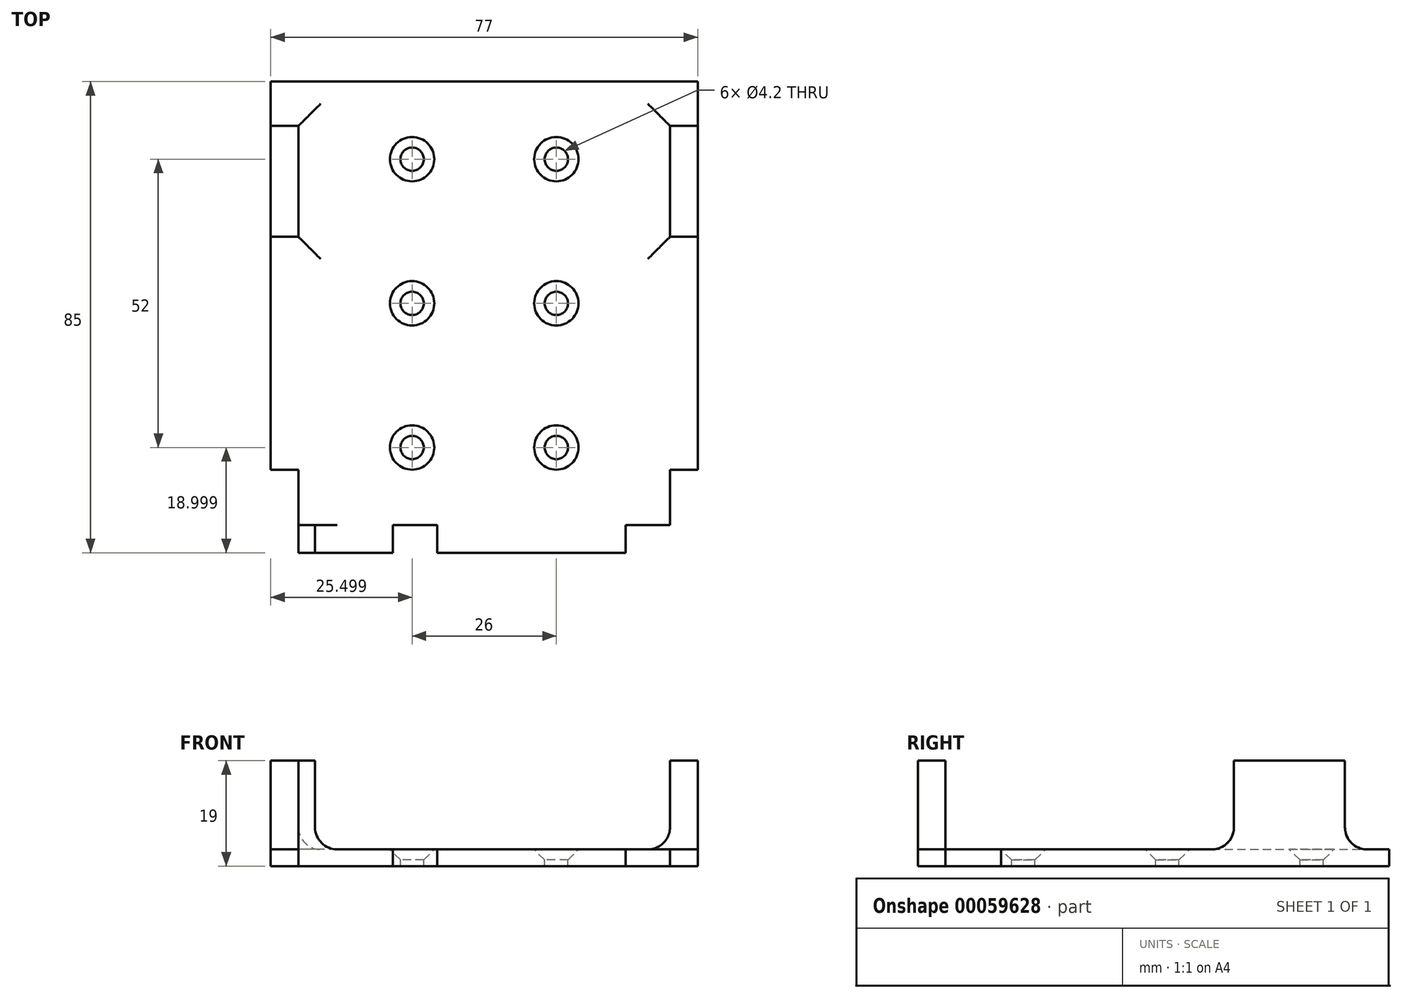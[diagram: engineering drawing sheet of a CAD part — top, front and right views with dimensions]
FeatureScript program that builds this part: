
annotation { "Feature Type Name" : "Feature", "Feature Type Description" : "" }
export const myFeature = defineFeature(function(context is Context, id is Id, definition is map)
    precondition{}
    {
        {
            var Q0;
            Q0=qCreatedBy(makeId("Top.planeOp"),FACE);
            var sketch = newSketch(context, id + "F0", { "sketchPlane" : qUnion([Q0])});
            skLineSegment(sketch, "E0.bottom", {"start": v(-19.43, 2.99) * mm, "end": v(57.57, 2.99) * mm});
            skLineSegment(sketch, "E0.top", {"start": v(-19.43, -82.01) * mm, "end": v(57.57, -82.01) * mm});
            skLineSegment(sketch, "E0.left", {"start": v(-19.43, 2.99) * mm, "end": v(-19.43, -82.01) * mm});
            skLineSegment(sketch, "E0.right", {"start": v(57.57, 2.99) * mm, "end": v(57.57, -82.01) * mm});
            skLineSegment(sketch, "E1.bottom", {"start": v(2.57, -82.01) * mm, "end": v(10.57, -82.01) * mm});
            skLineSegment(sketch, "E1.top", {"start": v(2.57, -77.01) * mm, "end": v(10.57, -77.01) * mm});
            skLineSegment(sketch, "E1.left", {"start": v(2.57, -82.01) * mm, "end": v(2.57, -77.01) * mm});
            skLineSegment(sketch, "E1.right", {"start": v(10.57, -82.01) * mm, "end": v(10.57, -77.01) * mm});
            skLineSegment(sketch, "E2.bottom", {"start": v(-19.43, -5.01) * mm, "end": v(-14.43, -5.01) * mm});
            skLineSegment(sketch, "E2.top", {"start": v(-19.43, -25.01) * mm, "end": v(-14.43, -25.01) * mm});
            skLineSegment(sketch, "E2.left", {"start": v(-19.43, -5.01) * mm, "end": v(-19.43, -25.01) * mm});
            skLineSegment(sketch, "E2.right", {"start": v(-14.43, -5.01) * mm, "end": v(-14.43, -25.01) * mm});
            skLineSegment(sketch, "E3.bottom", {"start": v(57.57, -5.01) * mm, "end": v(52.57, -5.01) * mm});
            skLineSegment(sketch, "E3.top", {"start": v(57.57, -25.01) * mm, "end": v(52.57, -25.01) * mm});
            skLineSegment(sketch, "E3.left", {"start": v(57.57, -5.01) * mm, "end": v(57.57, -25.01) * mm});
            skLineSegment(sketch, "E3.right", {"start": v(52.57, -5.01) * mm, "end": v(52.57, -25.01) * mm});
            skLineSegment(sketch, "E4", {"start": v(-14.43, -25.01) * mm, "end": v(-14.43, -108.86) * mm, "construction": true});
            skLineSegment(sketch, "E5", {"start": v(52.57, -25.01) * mm, "end": v(52.57, -106.5) * mm, "construction": true});
            skLineSegment(sketch, "E6", {"start": v(-41.42, -77.01) * mm, "end": v(97.95, -77.01) * mm, "construction": true});
            skPoint(sketch, "E7", {"position": v(-14.43, -77.01) * mm});
            skPoint(sketch, "E8", {"position": v(52.57, -77.01) * mm});
            skLineSegment(sketch, "E9.bottom", {"start": v(57.57, -82.01) * mm, "end": v(44.57, -82.01) * mm});
            skLineSegment(sketch, "E9.top", {"start": v(57.57, -77.01) * mm, "end": v(44.57, -77.01) * mm});
            skLineSegment(sketch, "E9.left", {"start": v(57.57, -82.01) * mm, "end": v(57.57, -77.01) * mm});
            skLineSegment(sketch, "E9.right", {"start": v(44.57, -82.01) * mm, "end": v(44.57, -77.01) * mm});
            skLineSegment(sketch, "E10.bottom", {"start": v(52.57, -77.01) * mm, "end": v(57.57, -77.01) * mm});
            skLineSegment(sketch, "E10.top", {"start": v(52.57, -67.01) * mm, "end": v(57.57, -67.01) * mm});
            skLineSegment(sketch, "E10.left", {"start": v(52.57, -77.01) * mm, "end": v(52.57, -67.01) * mm});
            skLineSegment(sketch, "E10.right", {"start": v(57.57, -77.01) * mm, "end": v(57.57, -67.01) * mm});
            skLineSegment(sketch, "E11.bottom", {"start": v(-19.43, -82.01) * mm, "end": v(-14.43, -82.01) * mm});
            skLineSegment(sketch, "E11.top", {"start": v(-19.43, -67.01) * mm, "end": v(-14.43, -67.01) * mm});
            skLineSegment(sketch, "E11.left", {"start": v(-19.43, -82.01) * mm, "end": v(-19.43, -67.01) * mm});
            skLineSegment(sketch, "E11.right", {"start": v(-14.43, -82.01) * mm, "end": v(-14.43, -67.01) * mm});
            skLineSegment(sketch, "E12.bottom", {"start": v(-14.43, -77.01) * mm, "end": v(-11.43, -77.01) * mm});
            skLineSegment(sketch, "E12.top", {"start": v(-14.43, -82.01) * mm, "end": v(-11.43, -82.01) * mm});
            skLineSegment(sketch, "E12.left", {"start": v(-14.43, -77.01) * mm, "end": v(-14.43, -82.01) * mm});
            skLineSegment(sketch, "E12.right", {"start": v(-11.43, -77.01) * mm, "end": v(-11.43, -82.01) * mm});
            skLineSegment(sketch, "E13", {"start": v(19.07, 2.99) * mm, "end": v(19.07, -82.01) * mm, "construction": true});
            skCircle(sketch, "E14", {"center": v(19.07, -11.01) * mm, "radius": 13 * mm, "construction": true});
            skCircle(sketch, "E15", {"center": v(6.07, -11.01) * mm, "radius": 1.6 * mm, "construction": true});
            skCircle(sketch, "E16", {"center": v(32.07, -11.01) * mm, "radius": 1.6 * mm, "construction": true});
            skCircle(sketch, "E17", {"center": v(19.07, -63.01) * mm, "radius": 13 * mm, "construction": true});
            skCircle(sketch, "E18", {"center": v(32.07, -63.01) * mm, "radius": 1.6 * mm, "construction": true});
            skCircle(sketch, "E19", {"center": v(6.07, -63.01) * mm, "radius": 1.6 * mm, "construction": true});
            skCircle(sketch, "E20", {"center": v(19.07, -37.01) * mm, "radius": 13 * mm, "construction": true});
            skLineSegment(sketch, "E21", {"start": v(6.07, -37.01) * mm, "end": v(32.07, -37.01) * mm, "construction": true});
            skCircle(sketch, "E22", {"center": v(6.07, -37.01) * mm, "radius": 1.6 * mm, "construction": true});
            skCircle(sketch, "E23", {"center": v(32.07, -37.01) * mm, "radius": 1.6 * mm, "construction": true});
            skSolve(sketch);
        }
        {
            var Q0;
            {var subQ7=sQuery(id+"F0.wireOp",EDGE,"E0.bottom");Q0=makeQuery(id+"F0.imprint","IMPRINT",FACE,{"disambiguationData":[TD([[makeQuery(id+"F0.imprint","IMPRINT",EDGE,{"derivedFrom":subQ7}),-1.0]])]});}
            var Q1;
            Q1=makeQuery(id+"F0.imprint","IMPRINT",FACE,{"disambiguationData":[TD([[makeQuery(id+"F0.imprint","IMPRINT",EDGE,{"derivedFrom":sQuery(id+"F0.wireOp",EDGE,"E1.bottom")}),1.0]])]});
            var Q2;
            Q2=makeQuery(id+"F0.imprint","IMPRINT",FACE,{"disambiguationData":[TD([[makeQuery(id+"F0.imprint","IMPRINT",EDGE,{"derivedFrom":sQuery(id+"F0.wireOp",EDGE,"E11.bottom")}),1.0]])]});
            var Q3;
            Q3=makeQuery(id+"F0.imprint","IMPRINT",FACE,{"disambiguationData":[TD([[makeQuery(id+"F0.imprint","IMPRINT",EDGE,{"derivedFrom":sQuery(id+"F0.wireOp",EDGE,"E12.bottom")}),-1.0]])]});
            var Q4;
            Q4=makeQuery(id+"F0.imprint","IMPRINT",FACE,{"disambiguationData":[TD([[makeQuery(id+"F0.imprint","IMPRINT",EDGE,{"derivedFrom":sQuery(id+"F0.wireOp",EDGE,"E9.bottom")}),-1.0]])]});
            var Q5;
            Q5=makeQuery(id+"F0.imprint","IMPRINT",FACE,{"disambiguationData":[TD([[makeQuery(id+"F0.imprint","IMPRINT",EDGE,{"derivedFrom":sQuery(id+"F0.wireOp",EDGE,"E10.bottom")}),1.0]])]});
            var Q6;
            Q6=makeQuery(id+"F0.imprint","IMPRINT",FACE,{"disambiguationData":[TD([[makeQuery(id+"F0.imprint","IMPRINT",EDGE,{"derivedFrom":sQuery(id+"F0.wireOp",EDGE,"E3.bottom")}),1.0]])]});
            var Q7;
            Q7=makeQuery(id+"F0.imprint","IMPRINT",FACE,{"disambiguationData":[TD([[makeQuery(id+"F0.imprint","IMPRINT",EDGE,{"derivedFrom":sQuery(id+"F0.wireOp",EDGE,"E2.bottom")}),-1.0]])]});
            extrude(context, id + "F1", {"entities" : qUnion([Q0, Q1, Q2, Q3, Q4, Q5, Q6, Q7]), "depth" : 3 * mm});
        }
        {
            var Q0;
            Q0=makeQuery(id+"F0.imprint","IMPRINT",FACE,{"disambiguationData":[TD([[makeQuery(id+"F0.imprint","IMPRINT",EDGE,{"derivedFrom":sQuery(id+"F0.wireOp",EDGE,"E2.bottom")}),-1.0]])]});
            var Q1;
            Q1=makeQuery(id+"F0.imprint","IMPRINT",FACE,{"disambiguationData":[TD([[makeQuery(id+"F0.imprint","IMPRINT",EDGE,{"derivedFrom":sQuery(id+"F0.wireOp",EDGE,"E3.bottom")}),1.0]])]});
            var Q2;
            Q2=makeQuery(id+"F0.imprint","IMPRINT",FACE,{"disambiguationData":[TD([[makeQuery(id+"F0.imprint","IMPRINT",EDGE,{"derivedFrom":sQuery(id+"F0.wireOp",EDGE,"E10.bottom")}),1.0]])]});
            var Q3;
            Q3=makeQuery(id+"F0.imprint","IMPRINT",FACE,{"disambiguationData":[TD([[makeQuery(id+"F0.imprint","IMPRINT",EDGE,{"derivedFrom":sQuery(id+"F0.wireOp",EDGE,"E9.bottom")}),-1.0]])]});
            var Q4;
            Q4=makeQuery(id+"F0.imprint","IMPRINT",FACE,{"disambiguationData":[TD([[makeQuery(id+"F0.imprint","IMPRINT",EDGE,{"derivedFrom":sQuery(id+"F0.wireOp",EDGE,"E1.bottom")}),1.0]])]});
            var Q5;
            Q5=makeQuery(id+"F0.imprint","IMPRINT",FACE,{"disambiguationData":[TD([[makeQuery(id+"F0.imprint","IMPRINT",EDGE,{"derivedFrom":sQuery(id+"F0.wireOp",EDGE,"E11.bottom")}),1.0]])]});
            var Q6;
            Q6=makeQuery(id+"F0.imprint","IMPRINT",FACE,{"disambiguationData":[TD([[makeQuery(id+"F0.imprint","IMPRINT",EDGE,{"derivedFrom":sQuery(id+"F0.wireOp",EDGE,"E12.bottom")}),-1.0]])]});
            extrude(context, id + "F2", {"entities" : qUnion([Q0, Q1, Q2, Q3, Q4, Q5, Q6]), "operationType" : NewBodyOperationType.ADD, "depth" : 19 * mm});
        }
        {
            var Q0;
            Q0=makeQuery(id+"F1.opExtrude","CAP_FACE",FACE,{"disambiguationData":[OSD([sQuery(id+"F0.wireOp",EDGE,"E0.bottom"),sQuery(id+"F0.wireOp",EDGE,"E0.top"),sQuery(id+"F0.wireOp",EDGE,"E0.left"),sQuery(id+"F0.wireOp",EDGE,"E0.right"),sQuery(id+"F0.wireOp",EDGE,"E1.bottom"),sQuery(id+"F0.wireOp",EDGE,"E2.left"),sQuery(id+"F0.wireOp",EDGE,"E3.left"),sQuery(id+"F0.wireOp",EDGE,"E9.bottom"),sQuery(id+"F0.wireOp",EDGE,"E9.left"),sQuery(id+"F0.wireOp",EDGE,"E10.right"),sQuery(id+"F0.wireOp",EDGE,"E11.bottom"),sQuery(id+"F0.wireOp",EDGE,"E11.left"),sQuery(id+"F0.wireOp",EDGE,"E12.top")])],"isStart":false});
            var sketch = newSketch(context, id + "F3", { "sketchPlane" : qUnion([Q0])});
            skPoint(sketch, "E24", {"position": v(6.07, -11.01) * mm});
            skPoint(sketch, "E25", {"position": v(32.07, -11.01) * mm});
            skPoint(sketch, "E26", {"position": v(6.07, -63.01) * mm});
            skPoint(sketch, "E27", {"position": v(32.07, -63.01) * mm});
            skPoint(sketch, "E28", {"position": v(6.07, -37.01) * mm});
            skPoint(sketch, "E29", {"position": v(32.07, -37.01) * mm});
            skSolve(sketch);
        }
        {
            var Q0;
            Q0=sQuery(id+"F3.wireOp",VERTEX,"E24");
            var Q1;
            Q1=sQuery(id+"F3.wireOp",VERTEX,"E25");
            var Q2;
            Q2=sQuery(id+"F3.wireOp",VERTEX,"E26");
            var Q3;
            Q3=sQuery(id+"F3.wireOp",VERTEX,"E27");
            var Q4;
            Q4=sQuery(id+"F3.wireOp",VERTEX,"E29");
            var Q5;
            Q5=sQuery(id+"F3.wireOp",VERTEX,"E28");
            var Q6;
            Q6=makeQuery(id+"F1.opExtrude","SWEPT_BODY",BODY,{"disambiguationData":[OSD([sQuery(id+"F0.wireOp",EDGE,"E0.bottom"),sQuery(id+"F0.wireOp",EDGE,"E0.top"),sQuery(id+"F0.wireOp",EDGE,"E0.left"),sQuery(id+"F0.wireOp",EDGE,"E0.right"),sQuery(id+"F0.wireOp",EDGE,"E1.bottom"),sQuery(id+"F0.wireOp",EDGE,"E2.left"),sQuery(id+"F0.wireOp",EDGE,"E3.left"),sQuery(id+"F0.wireOp",EDGE,"E9.bottom"),sQuery(id+"F0.wireOp",EDGE,"E9.left"),sQuery(id+"F0.wireOp",EDGE,"E10.right"),sQuery(id+"F0.wireOp",EDGE,"E11.bottom"),sQuery(id+"F0.wireOp",EDGE,"E11.left"),sQuery(id+"F0.wireOp",EDGE,"E12.top")])]});
            hole(context, id + "F4", {"style" : HoleStyle.C_SINK, "holeDiameter" : 4.2 * mm, "cSinkDiameter" : 8 * mm, "endStyle" : HoleEndStyle.THROUGH, "locations" : qUnion([Q0, Q1, Q2, Q3, Q4, Q5]), "scope" : qUnion([Q6]), "cSinkAngle" : 90 * degree, "tappedDepth" : 12 * mm, "tapClearance" : 3});
        }
        {
            var Q0;
            Q0=makeQuery(id+"F2.boolean.opBoolean","INTERSECT",EDGE,{"derivedFrom":[makeQuery(id+"F1.opExtrude","CAP_FACE",FACE,{"disambiguationData":[OSD([sQuery(id+"F0.wireOp",EDGE,"E0.bottom"),sQuery(id+"F0.wireOp",EDGE,"E0.top"),sQuery(id+"F0.wireOp",EDGE,"E0.left"),sQuery(id+"F0.wireOp",EDGE,"E0.right"),sQuery(id+"F0.wireOp",EDGE,"E1.bottom"),sQuery(id+"F0.wireOp",EDGE,"E2.left"),sQuery(id+"F0.wireOp",EDGE,"E3.left"),sQuery(id+"F0.wireOp",EDGE,"E9.bottom"),sQuery(id+"F0.wireOp",EDGE,"E9.left"),sQuery(id+"F0.wireOp",EDGE,"E10.right"),sQuery(id+"F0.wireOp",EDGE,"E11.bottom"),sQuery(id+"F0.wireOp",EDGE,"E11.left"),sQuery(id+"F0.wireOp",EDGE,"E12.top")])],"isStart":false}),makeQuery(id+"F2.opExtrude","SWEPT_FACE",FACE,{"disambiguationData":[OSD([sQuery(id+"F0.wireOp",EDGE,"E2.top")])]})]});
            var Q1;
            Q1=makeQuery(id+"F2.boolean.opBoolean","INTERSECT",EDGE,{"derivedFrom":[makeQuery(id+"F1.opExtrude","CAP_FACE",FACE,{"disambiguationData":[OSD([sQuery(id+"F0.wireOp",EDGE,"E0.bottom"),sQuery(id+"F0.wireOp",EDGE,"E0.top"),sQuery(id+"F0.wireOp",EDGE,"E0.left"),sQuery(id+"F0.wireOp",EDGE,"E0.right"),sQuery(id+"F0.wireOp",EDGE,"E1.bottom"),sQuery(id+"F0.wireOp",EDGE,"E2.left"),sQuery(id+"F0.wireOp",EDGE,"E3.left"),sQuery(id+"F0.wireOp",EDGE,"E9.bottom"),sQuery(id+"F0.wireOp",EDGE,"E9.left"),sQuery(id+"F0.wireOp",EDGE,"E10.right"),sQuery(id+"F0.wireOp",EDGE,"E11.bottom"),sQuery(id+"F0.wireOp",EDGE,"E11.left"),sQuery(id+"F0.wireOp",EDGE,"E12.top")])],"isStart":false}),makeQuery(id+"F2.opExtrude","SWEPT_FACE",FACE,{"disambiguationData":[OSD([sQuery(id+"F0.wireOp",EDGE,"E11.top")])]})]});
            var Q2;
            Q2=makeQuery(id+"F2.boolean.opBoolean","INTERSECT",EDGE,{"derivedFrom":[makeQuery(id+"F1.opExtrude","CAP_FACE",FACE,{"disambiguationData":[OSD([sQuery(id+"F0.wireOp",EDGE,"E0.bottom"),sQuery(id+"F0.wireOp",EDGE,"E0.top"),sQuery(id+"F0.wireOp",EDGE,"E0.left"),sQuery(id+"F0.wireOp",EDGE,"E0.right"),sQuery(id+"F0.wireOp",EDGE,"E1.bottom"),sQuery(id+"F0.wireOp",EDGE,"E2.left"),sQuery(id+"F0.wireOp",EDGE,"E3.left"),sQuery(id+"F0.wireOp",EDGE,"E9.bottom"),sQuery(id+"F0.wireOp",EDGE,"E9.left"),sQuery(id+"F0.wireOp",EDGE,"E10.right"),sQuery(id+"F0.wireOp",EDGE,"E11.bottom"),sQuery(id+"F0.wireOp",EDGE,"E11.left"),sQuery(id+"F0.wireOp",EDGE,"E12.top")])],"isStart":false}),makeQuery(id+"F2.opExtrude","SWEPT_FACE",FACE,{"disambiguationData":[OSD([sQuery(id+"F0.wireOp",EDGE,"E12.right")])]})]});
            var Q3;
            Q3=makeQuery(id+"F2.boolean.opBoolean","INTERSECT",EDGE,{"derivedFrom":[makeQuery(id+"F1.opExtrude","CAP_FACE",FACE,{"disambiguationData":[OSD([sQuery(id+"F0.wireOp",EDGE,"E0.bottom"),sQuery(id+"F0.wireOp",EDGE,"E0.top"),sQuery(id+"F0.wireOp",EDGE,"E0.left"),sQuery(id+"F0.wireOp",EDGE,"E0.right"),sQuery(id+"F0.wireOp",EDGE,"E1.bottom"),sQuery(id+"F0.wireOp",EDGE,"E2.left"),sQuery(id+"F0.wireOp",EDGE,"E3.left"),sQuery(id+"F0.wireOp",EDGE,"E9.bottom"),sQuery(id+"F0.wireOp",EDGE,"E9.left"),sQuery(id+"F0.wireOp",EDGE,"E10.right"),sQuery(id+"F0.wireOp",EDGE,"E11.bottom"),sQuery(id+"F0.wireOp",EDGE,"E11.left"),sQuery(id+"F0.wireOp",EDGE,"E12.top")])],"isStart":false}),makeQuery(id+"F2.opExtrude","SWEPT_FACE",FACE,{"disambiguationData":[OSD([sQuery(id+"F0.wireOp",EDGE,"E1.right")])]})]});
            var Q4;
            Q4=makeQuery(id+"F2.boolean.opBoolean","INTERSECT",EDGE,{"derivedFrom":[makeQuery(id+"F1.opExtrude","CAP_FACE",FACE,{"disambiguationData":[OSD([sQuery(id+"F0.wireOp",EDGE,"E0.bottom"),sQuery(id+"F0.wireOp",EDGE,"E0.top"),sQuery(id+"F0.wireOp",EDGE,"E0.left"),sQuery(id+"F0.wireOp",EDGE,"E0.right"),sQuery(id+"F0.wireOp",EDGE,"E1.bottom"),sQuery(id+"F0.wireOp",EDGE,"E2.left"),sQuery(id+"F0.wireOp",EDGE,"E3.left"),sQuery(id+"F0.wireOp",EDGE,"E9.bottom"),sQuery(id+"F0.wireOp",EDGE,"E9.left"),sQuery(id+"F0.wireOp",EDGE,"E10.right"),sQuery(id+"F0.wireOp",EDGE,"E11.bottom"),sQuery(id+"F0.wireOp",EDGE,"E11.left"),sQuery(id+"F0.wireOp",EDGE,"E12.top")])],"isStart":false}),makeQuery(id+"F2.opExtrude","SWEPT_FACE",FACE,{"disambiguationData":[OSD([sQuery(id+"F0.wireOp",EDGE,"E1.left")])]})]});
            var Q5;
            Q5=makeQuery(id+"F2.boolean.opBoolean","INTERSECT",EDGE,{"derivedFrom":[makeQuery(id+"F1.opExtrude","CAP_FACE",FACE,{"disambiguationData":[OSD([sQuery(id+"F0.wireOp",EDGE,"E0.bottom"),sQuery(id+"F0.wireOp",EDGE,"E0.top"),sQuery(id+"F0.wireOp",EDGE,"E0.left"),sQuery(id+"F0.wireOp",EDGE,"E0.right"),sQuery(id+"F0.wireOp",EDGE,"E1.bottom"),sQuery(id+"F0.wireOp",EDGE,"E2.left"),sQuery(id+"F0.wireOp",EDGE,"E3.left"),sQuery(id+"F0.wireOp",EDGE,"E9.bottom"),sQuery(id+"F0.wireOp",EDGE,"E9.left"),sQuery(id+"F0.wireOp",EDGE,"E10.right"),sQuery(id+"F0.wireOp",EDGE,"E11.bottom"),sQuery(id+"F0.wireOp",EDGE,"E11.left"),sQuery(id+"F0.wireOp",EDGE,"E12.top")])],"isStart":false}),makeQuery(id+"F2.opExtrude","SWEPT_FACE",FACE,{"disambiguationData":[OSD([sQuery(id+"F0.wireOp",EDGE,"E9.right")])]})]});
            var Q6;
            Q6=makeQuery(id+"F2.boolean.opBoolean","INTERSECT",EDGE,{"derivedFrom":[makeQuery(id+"F1.opExtrude","CAP_FACE",FACE,{"disambiguationData":[OSD([sQuery(id+"F0.wireOp",EDGE,"E0.bottom"),sQuery(id+"F0.wireOp",EDGE,"E0.top"),sQuery(id+"F0.wireOp",EDGE,"E0.left"),sQuery(id+"F0.wireOp",EDGE,"E0.right"),sQuery(id+"F0.wireOp",EDGE,"E1.bottom"),sQuery(id+"F0.wireOp",EDGE,"E2.left"),sQuery(id+"F0.wireOp",EDGE,"E3.left"),sQuery(id+"F0.wireOp",EDGE,"E9.bottom"),sQuery(id+"F0.wireOp",EDGE,"E9.left"),sQuery(id+"F0.wireOp",EDGE,"E10.right"),sQuery(id+"F0.wireOp",EDGE,"E11.bottom"),sQuery(id+"F0.wireOp",EDGE,"E11.left"),sQuery(id+"F0.wireOp",EDGE,"E12.top")])],"isStart":false}),makeQuery(id+"F2.opExtrude","SWEPT_FACE",FACE,{"disambiguationData":[OSD([sQuery(id+"F0.wireOp",EDGE,"E3.top")])]})]});
            var Q7;
            Q7=makeQuery(id+"F2.boolean.opBoolean","INTERSECT",EDGE,{"derivedFrom":[makeQuery(id+"F1.opExtrude","CAP_FACE",FACE,{"disambiguationData":[OSD([sQuery(id+"F0.wireOp",EDGE,"E0.bottom"),sQuery(id+"F0.wireOp",EDGE,"E0.top"),sQuery(id+"F0.wireOp",EDGE,"E0.left"),sQuery(id+"F0.wireOp",EDGE,"E0.right"),sQuery(id+"F0.wireOp",EDGE,"E1.bottom"),sQuery(id+"F0.wireOp",EDGE,"E2.left"),sQuery(id+"F0.wireOp",EDGE,"E3.left"),sQuery(id+"F0.wireOp",EDGE,"E9.bottom"),sQuery(id+"F0.wireOp",EDGE,"E9.left"),sQuery(id+"F0.wireOp",EDGE,"E10.right"),sQuery(id+"F0.wireOp",EDGE,"E11.bottom"),sQuery(id+"F0.wireOp",EDGE,"E11.left"),sQuery(id+"F0.wireOp",EDGE,"E12.top")])],"isStart":false}),makeQuery(id+"F2.opExtrude","SWEPT_FACE",FACE,{"disambiguationData":[OSD([sQuery(id+"F0.wireOp",EDGE,"E10.top")])]})]});
            var Q8;
            Q8=makeQuery(id+"F2.boolean.opBoolean","INTERSECT",EDGE,{"derivedFrom":[makeQuery(id+"F1.opExtrude","CAP_FACE",FACE,{"disambiguationData":[OSD([sQuery(id+"F0.wireOp",EDGE,"E0.bottom"),sQuery(id+"F0.wireOp",EDGE,"E0.top"),sQuery(id+"F0.wireOp",EDGE,"E0.left"),sQuery(id+"F0.wireOp",EDGE,"E0.right"),sQuery(id+"F0.wireOp",EDGE,"E1.bottom"),sQuery(id+"F0.wireOp",EDGE,"E2.left"),sQuery(id+"F0.wireOp",EDGE,"E3.left"),sQuery(id+"F0.wireOp",EDGE,"E9.bottom"),sQuery(id+"F0.wireOp",EDGE,"E9.left"),sQuery(id+"F0.wireOp",EDGE,"E10.right"),sQuery(id+"F0.wireOp",EDGE,"E11.bottom"),sQuery(id+"F0.wireOp",EDGE,"E11.left"),sQuery(id+"F0.wireOp",EDGE,"E12.top")])],"isStart":false}),makeQuery(id+"F2.opExtrude","SWEPT_FACE",FACE,{"disambiguationData":[OSD([sQuery(id+"F0.wireOp",EDGE,"E3.bottom")])]})]});
            var Q9;
            Q9=makeQuery(id+"F2.boolean.opBoolean","INTERSECT",EDGE,{"derivedFrom":[makeQuery(id+"F1.opExtrude","CAP_FACE",FACE,{"disambiguationData":[OSD([sQuery(id+"F0.wireOp",EDGE,"E0.bottom"),sQuery(id+"F0.wireOp",EDGE,"E0.top"),sQuery(id+"F0.wireOp",EDGE,"E0.left"),sQuery(id+"F0.wireOp",EDGE,"E0.right"),sQuery(id+"F0.wireOp",EDGE,"E1.bottom"),sQuery(id+"F0.wireOp",EDGE,"E2.left"),sQuery(id+"F0.wireOp",EDGE,"E3.left"),sQuery(id+"F0.wireOp",EDGE,"E9.bottom"),sQuery(id+"F0.wireOp",EDGE,"E9.left"),sQuery(id+"F0.wireOp",EDGE,"E10.right"),sQuery(id+"F0.wireOp",EDGE,"E11.bottom"),sQuery(id+"F0.wireOp",EDGE,"E11.left"),sQuery(id+"F0.wireOp",EDGE,"E12.top")])],"isStart":false}),makeQuery(id+"F2.opExtrude","SWEPT_FACE",FACE,{"disambiguationData":[OSD([sQuery(id+"F0.wireOp",EDGE,"E2.bottom")])]})]});
            var Q10;
            Q10=makeQuery(id+"F2.boolean.opBoolean","INTERSECT",EDGE,{"derivedFrom":[makeQuery(id+"F1.opExtrude","CAP_FACE",FACE,{"disambiguationData":[OSD([sQuery(id+"F0.wireOp",EDGE,"E0.bottom"),sQuery(id+"F0.wireOp",EDGE,"E0.top"),sQuery(id+"F0.wireOp",EDGE,"E0.left"),sQuery(id+"F0.wireOp",EDGE,"E0.right"),sQuery(id+"F0.wireOp",EDGE,"E1.bottom"),sQuery(id+"F0.wireOp",EDGE,"E2.left"),sQuery(id+"F0.wireOp",EDGE,"E3.left"),sQuery(id+"F0.wireOp",EDGE,"E9.bottom"),sQuery(id+"F0.wireOp",EDGE,"E9.left"),sQuery(id+"F0.wireOp",EDGE,"E10.right"),sQuery(id+"F0.wireOp",EDGE,"E11.bottom"),sQuery(id+"F0.wireOp",EDGE,"E11.left"),sQuery(id+"F0.wireOp",EDGE,"E12.top")])],"isStart":false}),makeQuery(id+"F2.opExtrude","SWEPT_FACE",FACE,{"disambiguationData":[OSD([sQuery(id+"F0.wireOp",EDGE,"E2.right")])]})]});
            var Q11;
            Q11=makeQuery(id+"F2.boolean.opBoolean","INTERSECT",EDGE,{"derivedFrom":[makeQuery(id+"F1.opExtrude","CAP_FACE",FACE,{"disambiguationData":[OSD([sQuery(id+"F0.wireOp",EDGE,"E0.bottom"),sQuery(id+"F0.wireOp",EDGE,"E0.top"),sQuery(id+"F0.wireOp",EDGE,"E0.left"),sQuery(id+"F0.wireOp",EDGE,"E0.right"),sQuery(id+"F0.wireOp",EDGE,"E1.bottom"),sQuery(id+"F0.wireOp",EDGE,"E2.left"),sQuery(id+"F0.wireOp",EDGE,"E3.left"),sQuery(id+"F0.wireOp",EDGE,"E9.bottom"),sQuery(id+"F0.wireOp",EDGE,"E9.left"),sQuery(id+"F0.wireOp",EDGE,"E10.right"),sQuery(id+"F0.wireOp",EDGE,"E11.bottom"),sQuery(id+"F0.wireOp",EDGE,"E11.left"),sQuery(id+"F0.wireOp",EDGE,"E12.top")])],"isStart":false}),makeQuery(id+"F2.opExtrude","SWEPT_FACE",FACE,{"disambiguationData":[OSD([sQuery(id+"F0.wireOp",EDGE,"E3.right")])]})]});
            fillet(context, id + "F5", {"entities" : qUnion([Q0, Q1, Q2, Q3, Q4, Q5, Q6, Q7, Q8, Q9, Q10, Q11]), "radius" : 4 * mm, "tangentPropagation" : true, "allowEdgeOverflow" : false});
        }
    });
